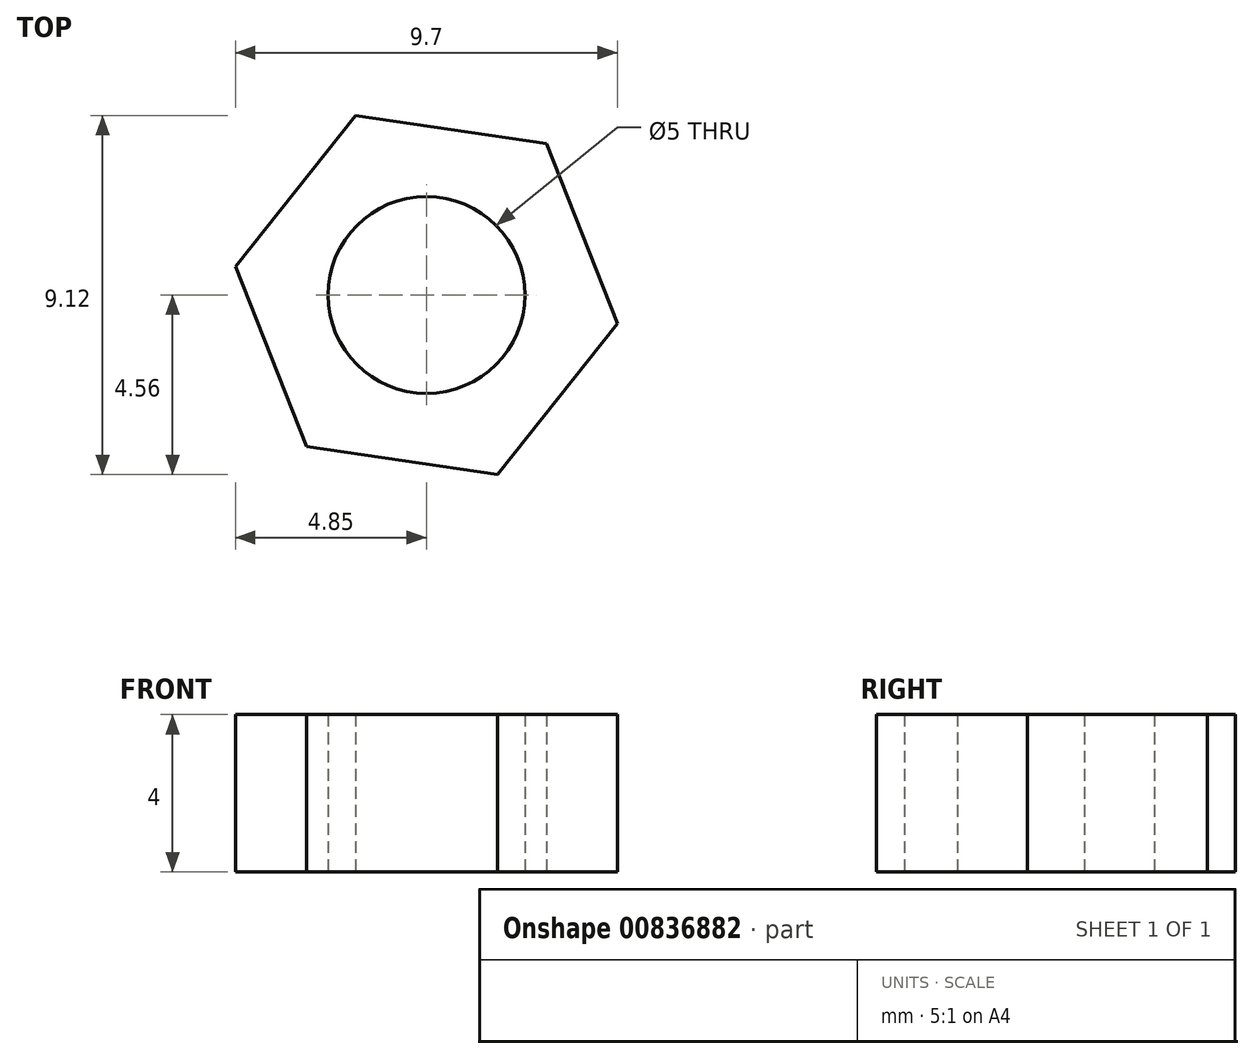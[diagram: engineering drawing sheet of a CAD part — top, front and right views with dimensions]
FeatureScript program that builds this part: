
annotation { "Feature Type Name" : "Feature", "Feature Type Description" : "" }
export const myFeature = defineFeature(function(context is Context, id is Id, definition is map)
    precondition{}
    {
        {
            var Q0;
            Q0=qCreatedBy(makeId("Top.planeOp"),FACE);
            var sketch = newSketch(context, id + "F0", { "sketchPlane" : qUnion([Q0])});
            skCircle(sketch, "E0.cCircle", {"center": v(0, 0) * mm, "radius": 4.25 * mm, "construction": true});
            skLineSegment(sketch, "E0.0", {"start": v(3.05, 3.84) * mm, "end": v(4.85, -0.72) * mm});
            skLineSegment(sketch, "E0.1", {"start": v(4.85, -0.72) * mm, "end": v(1.8, -4.56) * mm});
            skLineSegment(sketch, "E0.2", {"start": v(1.8, -4.56) * mm, "end": v(-3.05, -3.84) * mm});
            skLineSegment(sketch, "E0.3", {"start": v(-3.05, -3.84) * mm, "end": v(-4.85, 0.72) * mm});
            skLineSegment(sketch, "E0.4", {"start": v(-4.85, 0.72) * mm, "end": v(-1.8, 4.56) * mm});
            skLineSegment(sketch, "E0.5", {"start": v(-1.8, 4.56) * mm, "end": v(3.05, 3.84) * mm});
            skPoint(sketch, "E0.0.midPoint", {"position": v(3.95, 1.56) * mm});
            skCircle(sketch, "E1", {"center": v(0, 0) * mm, "radius": 2.5 * mm});
            skSolve(sketch);
        }
        {
            var Q0;
            Q0 = qSketchRegion(id + "F0", true);
            extrude(context, id + "F1", {"entities" : qUnion([Q0]), "depth" : 4 * mm, "offsetDistance" : 25.4 * mm});
        }
    });
